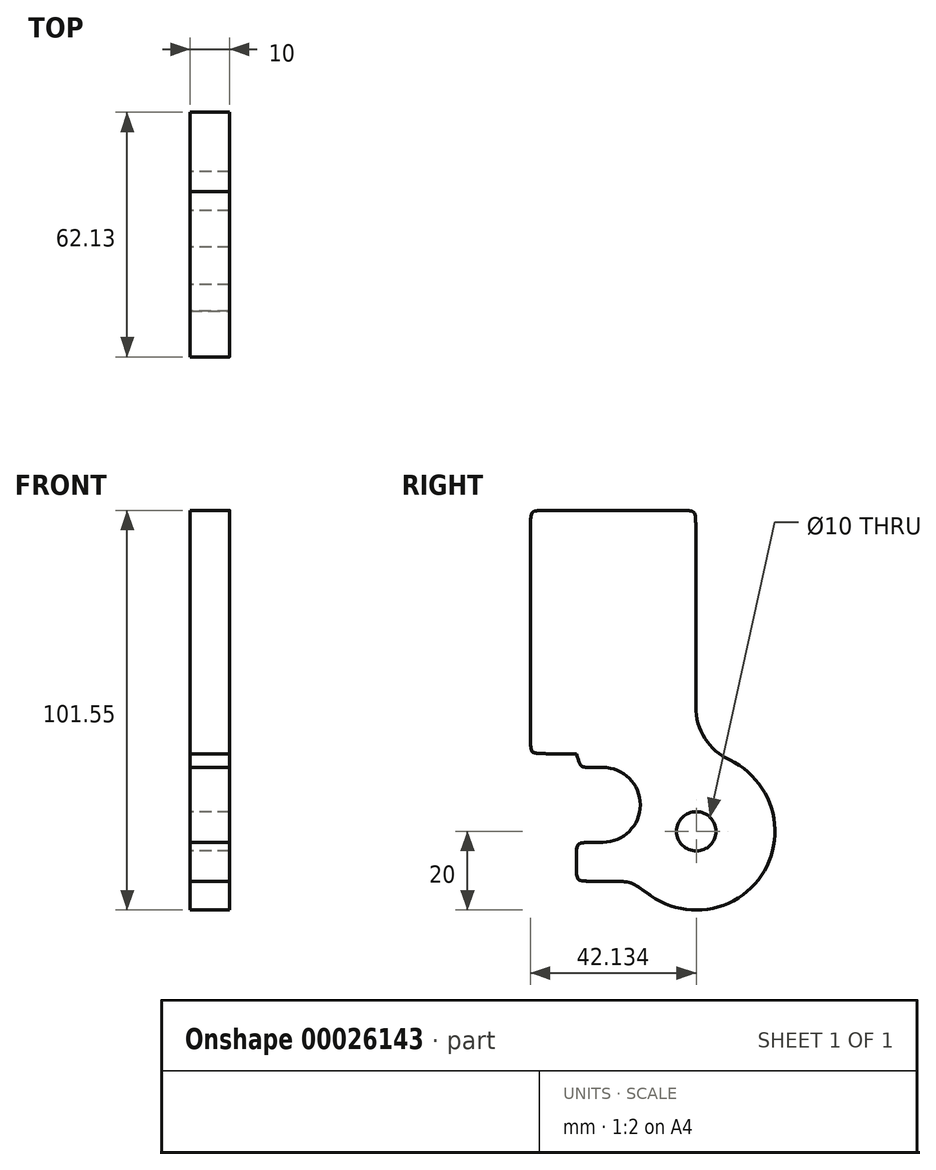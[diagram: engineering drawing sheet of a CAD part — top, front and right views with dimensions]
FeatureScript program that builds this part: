
annotation { "Feature Type Name" : "Feature", "Feature Type Description" : "" }
export const myFeature = defineFeature(function(context is Context, id is Id, definition is map)
    precondition{}
    {
        {
            var Q0;
            Q0=qCreatedBy(makeId("Right.planeOp"),FACE);
            var sketch = newSketch(context, id + "F0", { "sketchPlane" : qUnion([Q0])});
            skLineSegment(sketch, "E0.rect.bottom", {"start": v(45.56, -30.91) * mm, "end": v(-27.16, -30.91) * mm, "construction": true});
            skLineSegment(sketch, "E0.rect.top", {"start": v(45.56, 30.91) * mm, "end": v(-45.56, 30.91) * mm, "construction": true});
            skLineSegment(sketch, "E0.rect.left", {"start": v(45.56, -30.91) * mm, "end": v(45.56, 30.91) * mm, "construction": true});
            skLineSegment(sketch, "E0.rect.right", {"start": v(-45.56, -30.91) * mm, "end": v(-45.56, 30.91) * mm});
            skPoint(sketch, "E0.rect.middle", {"position": v(0, 0) * mm});
            skLineSegment(sketch, "E1", {"start": v(-3.43, 30.9) * mm, "end": v(-3.43, -30.9) * mm, "construction": true});
            skLineSegment(sketch, "E2", {"start": v(-45.56, 30.91) * mm, "end": v(-3.56, 30.91) * mm});
            skLineSegment(sketch, "E3", {"start": v(-27.06, 30.91) * mm, "end": v(-27.06, -30.91) * mm, "construction": true});
            skLineSegment(sketch, "E4", {"start": v(-45.56, -50.64) * mm, "end": v(45.56, -50.64) * mm, "construction": true});
            skLineSegment(sketch, "E5", {"start": v(-45.56, 0) * mm, "end": v(45.56, 0) * mm, "construction": true});
            skLineSegment(sketch, "E6", {"start": v(-3.43, 30.9) * mm, "end": v(-3.43, -89.73) * mm, "construction": true});
            skCircle(sketch, "E7", {"center": v(-3.43, -50.64) * mm, "radius": 5 * mm});
            skLineSegment(sketch, "E8", {"start": v(-45.56, -30.91) * mm, "end": v(-33.9, -30.91) * mm});
            skLineSegment(sketch, "E9", {"start": v(-27.16, -63.33) * mm, "end": v(-18.89, -63.33) * mm});
            skLineSegment(sketch, "E10.trimOffspring", {"start": v(44.58, 0) * mm, "end": v(45.56, -0.6) * mm});
            skLineSegment(sketch, "E11", {"start": v(-27.16, 30.9) * mm, "end": v(-27.16, -53.44) * mm, "construction": true});
            skLineSegment(sketch, "E12", {"start": v(-45.56, -43.91) * mm, "end": v(73.95, -43.9) * mm, "construction": true});
            skArc(sketch, "E13", {"start": v(-27.16, -53.41) * mm, "mid": v(-17.66, -43.91) * mm, "end": v(-27.16, -34.41) * mm});
            skLineSegment(sketch, "E14", {"start": v(-27.16, -30.91) * mm, "end": v(-27.06, -30.91) * mm});
            skLineSegment(sketch, "E15", {"start": v(-27.16, -53.41) * mm, "end": v(-27.16, -53.44) * mm});
            skLineSegment(sketch, "E16", {"start": v(-45.56, -53.44) * mm, "end": v(-35.95, -53.44) * mm, "construction": true});
            skLineSegment(sketch, "E17", {"start": v(-33.9, -63.33) * mm, "end": v(-27.16, -63.33) * mm});
            skLineSegment(sketch, "E18.trimOffspring", {"start": v(-27.16, -63.33) * mm, "end": v(-27.16, -100.76) * mm, "construction": true});
            skLineSegment(sketch, "E19", {"start": v(-33.9, -53.44) * mm, "end": v(-33.9, -63.33) * mm});
            skPoint(sketch, "E20.orphan", {"position": v(-24.43, -63.33) * mm});
            skLineSegment(sketch, "E21.trimOffspring", {"start": v(-33.9, -53.44) * mm, "end": v(54.22, -53.44) * mm, "construction": true});
            skLineSegment(sketch, "E22", {"start": v(-33.9, -53.44) * mm, "end": v(-27.16, -53.44) * mm});
            skLineSegment(sketch, "E23", {"start": v(-33.9, -30.91) * mm, "end": v(-33.9, -34.41) * mm});
            skLineSegment(sketch, "E24", {"start": v(-33.9, -34.41) * mm, "end": v(-27.16, -34.41) * mm});
            skLineSegment(sketch, "E25.trimOffspring", {"start": v(-33.9, -30.91) * mm, "end": v(-45.56, -30.91) * mm, "construction": true});
            skLineSegment(sketch, "E26", {"start": v(-3.56, 30.91) * mm, "end": v(-3.56, -18.96) * mm});
            skArc(sketch, "E27.trimOffspring", {"start": v(-18.89, -63.33) * mm, "mid": v(12.36, -62.92) * mm, "end": v(5.07, -32.53) * mm});
            skPoint(sketch, "E28.visualSharp", {"position": v(-3.56, -30.64) * mm});
            skArc(sketch, "E28.filletArc", {"start": v(-3.56, -18.96) * mm, "mid": v(-1.22, -27) * mm, "end": v(5.07, -32.53) * mm});
            skSolve(sketch);
        }
        {
            var Q0;
            Q0=makeQuery(id+"F0.imprint","IMPRINT",FACE,{"disambiguationData":[TD([[makeQuery(id+"F0.imprint","IMPRINT",EDGE,{"derivedFrom":sQuery(id+"F0.wireOp",EDGE,"E0.rect.right")}),-1.0]])]});
            extrude(context, id + "F1", {"entities" : qUnion([Q0]), "depth" : 10 * mm});
        }
        {
            var Q0;
            Q0=makeQuery(id+"F1.opExtrude","SWEPT_EDGE",EDGE,{"disambiguationData":[OSD([sQuery(id+"F0.wireOp",EDGE,"E23"),sQuery(id+"F0.wireOp",EDGE,"E24")])]});
            var Q1;
            Q1=makeQuery(id+"F1.opExtrude","SWEPT_EDGE",EDGE,{"disambiguationData":[OSD([sQuery(id+"F0.wireOp",EDGE,"E19"),sQuery(id+"F0.wireOp",EDGE,"E22")])]});
            var Q2;
            Q2=makeQuery(id+"F1.opExtrude","SWEPT_EDGE",EDGE,{"disambiguationData":[OSD([sQuery(id+"F0.wireOp",EDGE,"E17"),sQuery(id+"F0.wireOp",EDGE,"E19")])]});
            var Q3;
            Q3=makeQuery(id+"F1.opExtrude","SWEPT_EDGE",EDGE,{"disambiguationData":[OSD([sQuery(id+"F0.wireOp",EDGE,"E2"),sQuery(id+"F0.wireOp",EDGE,"ef8688d2-f183-422a-985d-0b9c50319a7e")])]});
            var Q4;
            Q4=makeQuery(id+"F1.opExtrude","SWEPT_EDGE",EDGE,{"disambiguationData":[OSD([sQuery(id+"F0.wireOp",EDGE,"E0.rect.right"),sQuery(id+"F0.wireOp",EDGE,"E8")])]});
            var Q5;
            Q5=makeQuery(id+"F1.opExtrude","SWEPT_EDGE",EDGE,{"disambiguationData":[OSD([sQuery(id+"F0.wireOp",EDGE,"E0.rect.right"),sQuery(id+"F0.wireOp",EDGE,"E2")])]});
            fillet(context, id + "F2", {"entities" : qUnion([Q0, Q1, Q2, Q3, Q4, Q5]), "radius" : 5 * mm, "tangentPropagation" : true, "rho" : 0.8, "crossSection" : FilletCrossSection.CONIC, "allowEdgeOverflow" : false});
        }
        {
            var Q0;
            Q0=makeQuery(id+"F1.opExtrude","SWEPT_EDGE",EDGE,{"disambiguationData":[OSD([sQuery(id+"F0.wireOp",EDGE,"E9"),sQuery(id+"F0.wireOp",EDGE,"ef8688d2-f183-422a-985d-0b9c50319a7e")])]});
            fillet(context, id + "F3", {"entities" : qUnion([Q0]), "radius" : 20 * mm, "tangentPropagation" : true, "rho" : 0.8, "crossSection" : FilletCrossSection.CONIC, "allowEdgeOverflow" : false});
        }
    });
